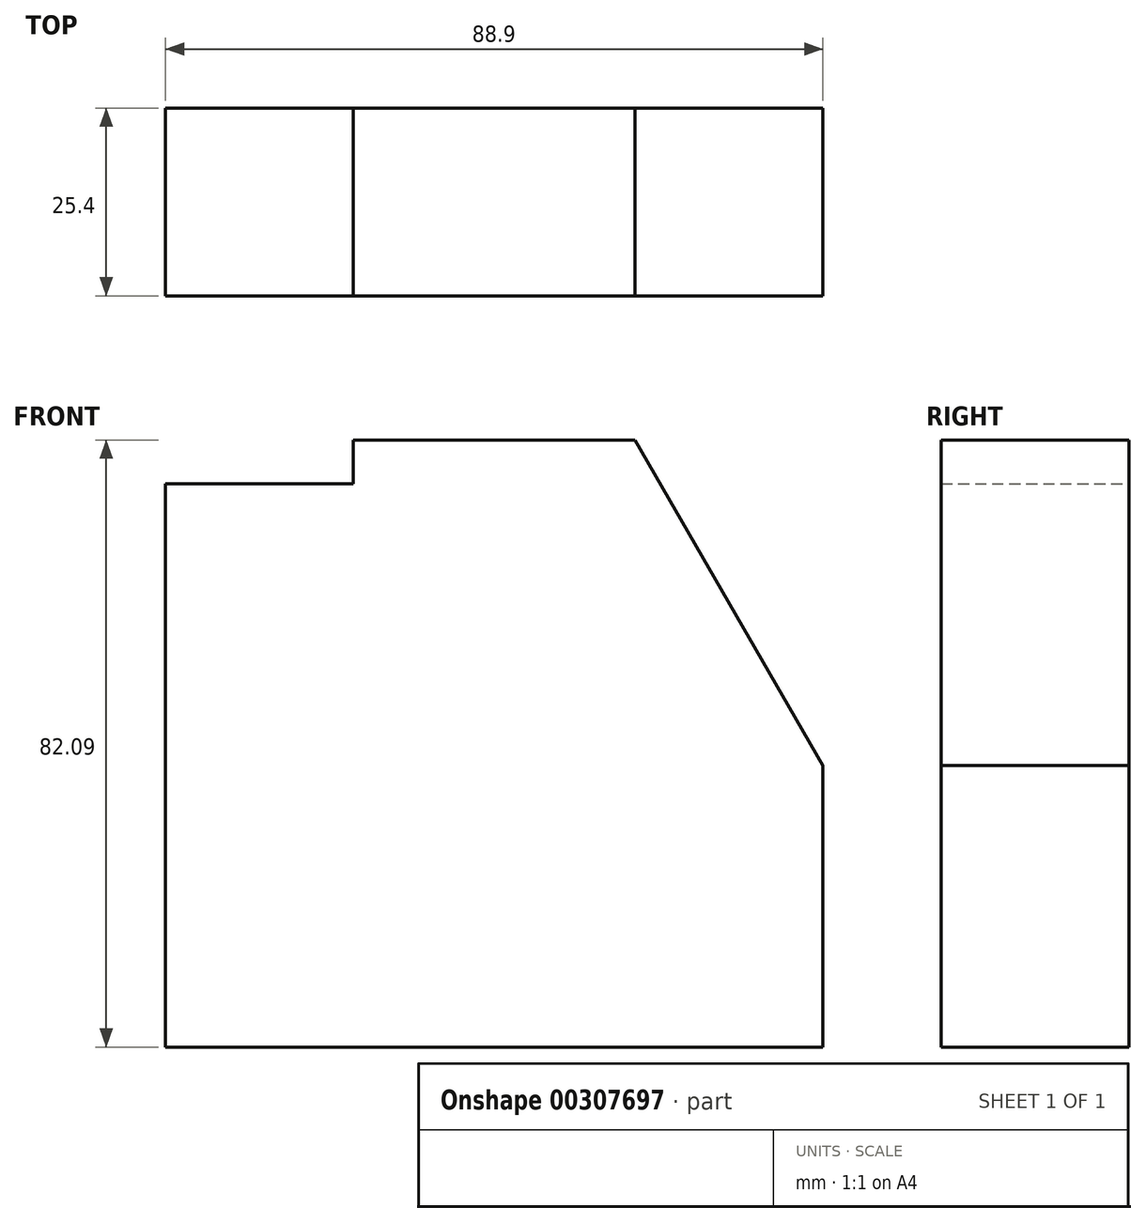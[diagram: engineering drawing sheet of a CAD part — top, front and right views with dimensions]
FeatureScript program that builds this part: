
annotation { "Feature Type Name" : "Feature", "Feature Type Description" : "" }
export const myFeature = defineFeature(function(context is Context, id is Id, definition is map)
    precondition{}
    {
        {
            var Q0;
            Q0=qCreatedBy(makeId("Front.planeOp"),FACE);
            var sketch = newSketch(context, id + "F0", { "sketchPlane" : qUnion([Q0])});
            skLineSegment(sketch, "E0", {"start": v(-54.5, -75.1) * mm, "end": v(34.4, -75.1) * mm});
            skLineSegment(sketch, "E1", {"start": v(34.4, -75.1) * mm, "end": v(34.4, -37) * mm});
            skLineSegment(sketch, "E2", {"start": v(34.4, -37) * mm, "end": v(9, 6.98) * mm});
            skLineSegment(sketch, "E3", {"start": v(9, 6.98) * mm, "end": v(-29.1, 6.98) * mm});
            skLineSegment(sketch, "E4", {"start": v(-29.1, 6.98) * mm, "end": v(-29.1, 1.1) * mm});
            skLineSegment(sketch, "E5", {"start": v(-29.1, 1.1) * mm, "end": v(-54.5, 1.1) * mm});
            skLineSegment(sketch, "E6", {"start": v(-54.5, 1.1) * mm, "end": v(-54.5, -75.1) * mm});
            skSolve(sketch);
        }
        {
            var Q0;
            Q0=makeQuery(id+"F0.imprint","IMPRINT",FACE,{"disambiguationData":[TD([[makeQuery(id+"F0.imprint","IMPRINT",EDGE,{"derivedFrom":sQuery(id+"F0.wireOp",EDGE,"E0")}),1.0]])]});
            extrude(context, id + "F1", {"entities" : qUnion([Q0]), "depth" : 25.4 * mm});
        }
    });
